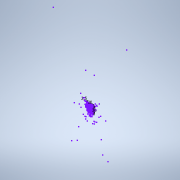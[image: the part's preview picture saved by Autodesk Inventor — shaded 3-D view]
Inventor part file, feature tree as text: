
AUTODESK INVENTOR PART (.ipt)
format: ipt  version: 2021.5 (Build 255421000, 421)  size: 881,152 bytes
history: native  units: mm
features: sketch x1
ambient origin geometry x8: Origin, YZ Plane, XZ Plane, XY Plane, X Axis, Y Axis, Z Axis, Center Point
feature tree (1):
  sketch  "Boceto2"  dims[d0=30.0mm d1=36.0mm d2=2.5mm]
